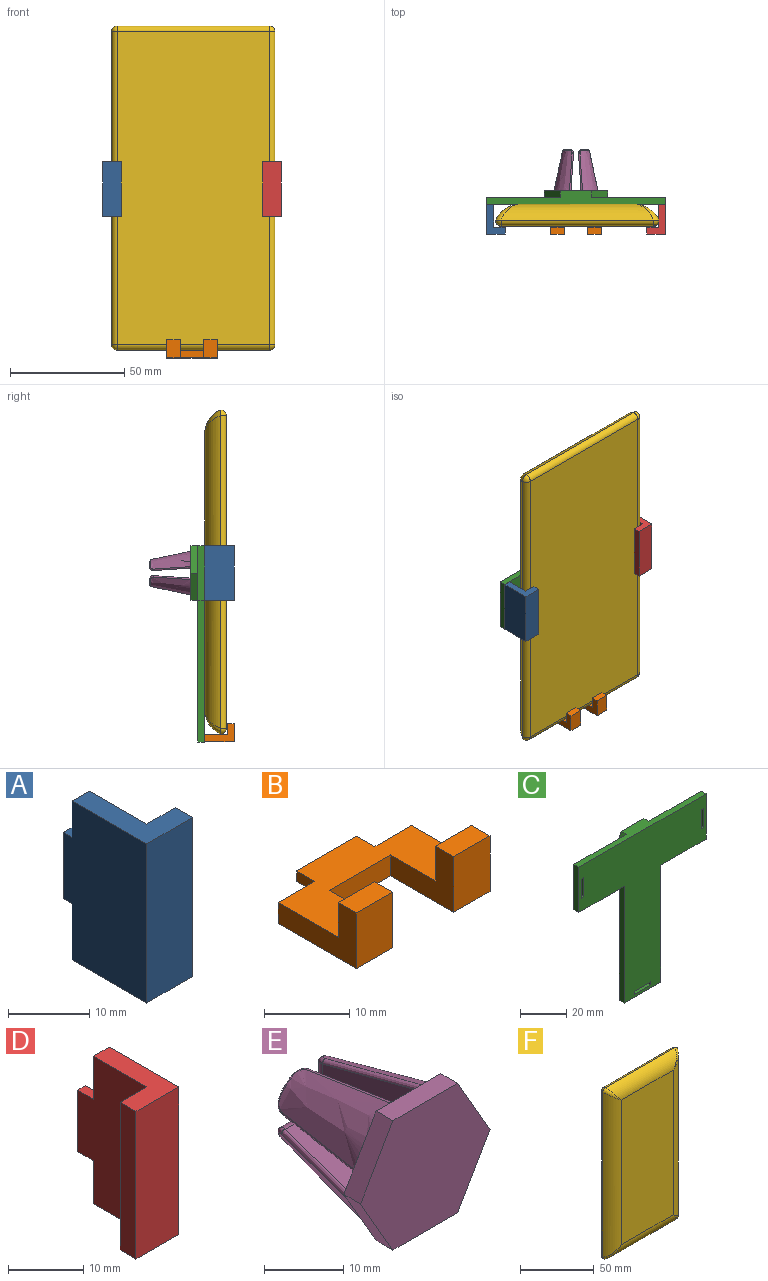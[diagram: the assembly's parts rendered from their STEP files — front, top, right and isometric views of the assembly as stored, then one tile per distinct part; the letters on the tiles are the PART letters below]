
ASSEMBLY  parts=6 mates=5
PART A: 12 faces, bbox 8x16x24 mm
  f0: plane 13x8mm, normal (0,0,-1), area 54mm2, adj f1,f4,f5,f6,f7,f11
  f1: plane 24x13mm, normal (1,0,0), area 270mm2, adj f0,f2,f3,f7,f8,f10,f11
  f2: plane 13x8mm, normal (0,0,1), area 54mm2, adj f1,f4,f5,f6,f7,f11
  f3: plane 10x1.5mm, normal (0,1,0), area 15mm2, adj f1,f8,f9,f10
  f4: plane 24x13mm, normal (-1,0,0), area 312mm2, adj f0,f2,f6,f11
  f5: plane 24x3mm, normal (1,0,0), area 72mm2, adj f0,f2,f6,f7
  f6: plane 24x8mm, normal (0,-1,0), area 192mm2, adj f0,f2,f4,f5
  f7: plane 24x5mm, normal (0,1,0), area 120mm2, adj f0,f1,f2,f5
  f8: plane 3x1.5mm, normal (0,0,1), area 4.5mm2, adj f1,f3,f9,f11
  f9: plane 10x3mm, normal (-1,0,0), area 30mm2, adj f3,f8,f10,f11
  f10: plane 3x1.5mm, normal (0,0,-1), area 4.5mm2, adj f1,f3,f9,f11
  f11: plane 24x3mm, normal (0,1,0), area 57mm2, adj f0,f1,f2,f4,f8,f9,f10
PART B: 18 faces, bbox 22.2x16x8 mm
  f0: plane 10x1.5mm, normal (0,1,0), area 15mm2, adj f1,f2,f3,f4
  f1: plane 22.2x13mm, normal (0,0,1), area 175.5mm2, adj f0,f3,f4,f5,f6,f7,f9,f12
  f2: plane 10x3mm, normal (0,0,-1), area 30mm2, adj f0,f3,f4,f5
  f3: plane 3x1.5mm, normal (-1,0,0), area 4.5mm2, adj f0,f1,f2,f5
  f4: plane 3x1.5mm, normal (1,0,0), area 4.5mm2, adj f0,f1,f2,f5
  f5: plane 22.2x3mm, normal (0,1,0), area 51.6mm2, adj f1,f2,f3,f4,f7,f8,f16
  f6: plane 10.5x8mm, normal (1,0,0), area 46.5mm2, adj f1,f8,f9,f10,f11,f17
  f7: plane 13x8mm, normal (-1,0,0), area 54mm2, adj f1,f5,f8,f9,f10,f11
  f8: plane 22.2x13mm, normal (0,0,-1), area 181.5mm2, adj f5,f6,f7,f11,f12,f15,f16,f17
  f9: plane 6x5mm, normal (0,1,0), area 30mm2, adj f1,f6,f7,f10
  f10: plane 6x3mm, normal (0,0,1), area 18mm2, adj f6,f7,f9,f11
  f11: plane 8x6mm, normal (0,-1,0), area 48mm2, adj f6,f7,f8,f10
  f12: plane 10.5x8mm, normal (-1,0,0), area 46.5mm2, adj f1,f8,f13,f14,f15,f17
  f13: plane 6x5mm, normal (0,1,0), area 30mm2, adj f1,f12,f14,f16
  f14: plane 6x3mm, normal (0,0,1), area 18mm2, adj f12,f13,f15,f16
  f15: plane 8x6mm, normal (0,-1,0), area 48mm2, adj f8,f12,f14,f16
  f16: plane 13x8mm, normal (1,0,0), area 54mm2, adj f1,f5,f8,f13,f14,f15
  f17: plane 10.2x3mm, normal (0,-1,0), area 30.6mm2, adj f1,f6,f8,f12
PART C: 35 faces, bbox 78.1x6x86 mm
  f0: plane 62x3mm, normal (-1,0,0), area 186mm2, adj f2,f3,f4,f5
  f1: plane 62x3mm, normal (1,0,0), area 186mm2, adj f2,f3,f4,f9
  f2: plane 22.2x3mm, normal (0,0,-1), area 66.6mm2, adj f0,f1,f3,f4
  f3: plane 86x78.1mm, normal (0,1,0), area 2703.5mm2, adj f0,f1,f2,f5,f6,f7,f8,f9
  f4: plane 86x78.1mm, normal (0,-1,0), area 3202.3mm2, adj f0,f1,f2,f5,f6,f7,f8,f9
  f5: plane 27.95x3mm, normal (0,0,-1), area 83.8mm2, adj f0,f3,f4,f8
  f6: plane 24x3mm, normal (1,0,0), area 72mm2, adj f3,f4,f7,f9
  f7: plane 78.1x6mm, normal (0,0,1), area 275.9mm2, adj f3,f4,f6,f8,f16,f17,f21
  f8: plane 24x3mm, normal (-1,0,0), area 72mm2, adj f3,f4,f5,f7
  f9: plane 27.95x3mm, normal (0,0,-1), area 83.8mm2, adj f1,f3,f4,f6
  f10: plane 10.1x5.83mm, normal (0.87,0,-0.5), area 35mm2, adj f11,f20,f21,f22
  f11: plane 10.1x5.83mm, normal (0.87,0,0.5), area 35mm2, adj f10,f12,f21,f22
  f12: plane 11.66x3mm, normal (0,0,1), area 35mm2, adj f11,f13,f21,f22
  f13: plane 10.1x5.83mm, normal (-0.87,0,0.5), area 35mm2, adj f12,f14,f21,f22
  f14: plane 10.1x5.83mm, normal (-0.87,0,-0.5), area 35mm2, adj f13,f20,f21,f22
  f15: plane 12x6.93mm, normal (-0.87,0,-0.5), area 41.6mm2, adj f3,f16,f19,f21
  f16: plane 12x6.93mm, normal (-0.87,0,0.5), area 41.6mm2, adj f3,f7,f15,f21
  f17: plane 12x6.93mm, normal (0.87,0,0.5), area 41.6mm2, adj f3,f7,f18,f21
  f18: plane 12x6.93mm, normal (0.87,0,-0.5), area 41.6mm2, adj f3,f17,f19,f21
  f19: plane 13.86x3mm, normal (0,0,-1), area 41.6mm2, adj f3,f15,f18,f21
  f20: plane 11.66x3mm, normal (0,0,-1), area 35mm2, adj f10,f14,f21,f22
  f21: plane 27.71x24mm, normal (0,1,0), area 145.5mm2, adj f7,f10,f11,f12,f13,f14,f15,f16
  f22: plane 23.33x20.2mm, normal (0,1,0), area 353.4mm2, adj f10,f11,f12,f13,f14,f20
  f23: plane 10.1x3mm, normal (1,0,0), area 30.3mm2, adj f3,f4,f24,f25
  f24: plane 3x1.6mm, normal (0,0,-1), area 4.8mm2, adj f3,f4,f23,f26
  f25: plane 3x1.6mm, normal (0,0,1), area 4.8mm2, adj f3,f4,f23,f26
  f26: plane 10.1x3mm, normal (-1,0,0), area 30.3mm2, adj f3,f4,f24,f25
  f27: plane 10.1x3mm, normal (0,0,1), area 30.3mm2, adj f3,f4,f28,f29
  f28: plane 3x1.6mm, normal (1,0,0), area 4.8mm2, adj f3,f4,f27,f30
  f29: plane 3x1.6mm, normal (-1,0,0), area 4.8mm2, adj f3,f4,f27,f30
  f30: plane 10.1x3mm, normal (0,0,-1), area 30.3mm2, adj f3,f4,f28,f29
  f31: plane 10.1x3mm, normal (1,0,0), area 30.3mm2, adj f3,f4,f32,f33
  f32: plane 3x1.6mm, normal (0,0,-1), area 4.8mm2, adj f3,f4,f31,f34
  f33: plane 3x1.6mm, normal (0,0,1), area 4.8mm2, adj f3,f4,f31,f34
  f34: plane 10.1x3mm, normal (-1,0,0), area 30.3mm2, adj f3,f4,f32,f33
PART D: 12 faces, bbox 8x16x24 mm
  f0: plane 13x8mm, normal (0,0,-1), area 54mm2, adj f1,f3,f5,f6,f7,f11
  f1: plane 24x13mm, normal (1,0,0), area 312mm2, adj f0,f4,f6,f11
  f2: plane 10x1.5mm, normal (0,1,0), area 15mm2, adj f3,f8,f9,f10
  f3: plane 24x13mm, normal (-1,0,0), area 270mm2, adj f0,f2,f4,f7,f8,f10,f11
  f4: plane 13x8mm, normal (0,0,1), area 54mm2, adj f1,f3,f5,f6,f7,f11
  f5: plane 24x3mm, normal (-1,0,0), area 72mm2, adj f0,f4,f6,f7
  f6: plane 24x8mm, normal (0,-1,0), area 192mm2, adj f0,f1,f4,f5
  f7: plane 24x5mm, normal (0,1,0), area 120mm2, adj f0,f3,f4,f5
  f8: plane 3x1.5mm, normal (0,0,-1), area 4.5mm2, adj f2,f3,f9,f11
  f9: plane 10x3mm, normal (1,0,0), area 30mm2, adj f2,f8,f10,f11
  f10: plane 3x1.5mm, normal (0,0,1), area 4.5mm2, adj f2,f3,f9,f11
  f11: plane 24x3mm, normal (0,1,0), area 57mm2, adj f0,f1,f3,f4,f8,f9,f10
PART E: 60 faces, bbox 23.2x23.4x20.6 mm
  f0: bspline ~17.61x8.12mm, area 143.4mm2, adj f4,f18,f19,f20,f48,f52
  f1: bspline ~17.61x8.12mm, area 143.4mm2, adj f4,f22,f23,f24,f43,f47
  f2: bspline ~17.61x8.12mm, area 143.4mm2, adj f4,f26,f27,f28,f38,f42
  f3: bspline ~17.61x8.12mm, area 143.4mm2, adj f4,f30,f31,f32,f33,f37
  f4: plane 23.15x20.06mm, normal (0,1,0), area 188.5mm2, adj f0,f1,f2,f3,f6,f7,f9,f10
  f5: plane 2.36x2.36mm, normal (0,1,0), area 3.3mm2, adj f31,f34,f36
  f6: plane 16.4x7.48mm, normal (-1,-0.07,0), area 85.4mm2, adj f4,f29,f32,f34
  f7: plane 16.4x7.48mm, normal (0,-0.07,-1), area 85.4mm2, adj f4,f29,f30,f36
  f8: plane 2.36x2.36mm, normal (0,1,0), area 3.3mm2, adj f27,f39,f41
  f9: plane 16.4x7.48mm, normal (1,-0.07,0), area 85.4mm2, adj f4,f25,f28,f39
  f10: plane 16.4x7.48mm, normal (0,-0.07,-1), area 85.4mm2, adj f4,f25,f26,f41
  f11: plane 2.36x2.36mm, normal (0,1,0), area 3.3mm2, adj f23,f44,f46
  f12: plane 16.4x7.48mm, normal (-1,-0.07,0), area 85.4mm2, adj f4,f21,f24,f44
  f13: plane 16.4x7.48mm, normal (0,-0.07,1), area 85.4mm2, adj f4,f21,f22,f46
  f14: plane 2.36x2.36mm, normal (0,1,0), area 3.3mm2, adj f19,f49,f51
  f15: plane 16.4x7.48mm, normal (0,-0.07,1), area 85.4mm2, adj f4,f17,f20,f49
  f16: plane 16.4x7.48mm, normal (1,-0.07,0), area 85.4mm2, adj f4,f17,f18,f51
  f17: cylinder r=0.5mm len=16.41mm, axis (-0.07,-1,-0.07), area 12.9mm2, adj f4,f15,f16,f50
  f18: bspline ~22.72x5.45mm, area 15.7mm2, adj f0,f4,f16,f52
  f19: bspline ~3.89x3.54mm, area 2.4mm2, adj f0,f14,f48,f52
  f20: bspline ~22.72x5.45mm, area 15.7mm2, adj f0,f4,f15,f48
  f21: cylinder r=0.5mm len=16.41mm, axis (0.07,-1,-0.07), area 12.9mm2, adj f4,f12,f13,f45
  f22: bspline ~22.72x5.45mm, area 15.7mm2, adj f1,f4,f13,f47
  f23: bspline ~3.89x3.54mm, area 2.4mm2, adj f1,f11,f43,f47
  f24: bspline ~22.72x5.45mm, area 15.7mm2, adj f1,f4,f12,f43
  f25: cylinder r=0.5mm len=16.41mm, axis (-0.07,-1,0.07), area 12.9mm2, adj f4,f9,f10,f40
  f26: bspline ~22.72x5.45mm, area 15.7mm2, adj f2,f4,f10,f42
  f27: bspline ~3.89x3.54mm, area 2.4mm2, adj f2,f8,f38,f42
  f28: bspline ~22.72x5.45mm, area 15.7mm2, adj f2,f4,f9,f38
  f29: cylinder r=0.5mm len=16.41mm, axis (-0.07,1,-0.07), area 12.9mm2, adj f4,f6,f7,f35
  f30: bspline ~20.18x4.91mm, area 15.7mm2, adj f3,f4,f7,f37
  f31: bspline ~3.62x3.43mm, area 2.4mm2, adj f3,f5,f33,f37
  f32: bspline ~20.18x4.91mm, area 15.7mm2, adj f3,f4,f6,f33
  f33: bspline ~2.03x1.75mm, area 1.9mm2, adj f3,f31,f32,f34
  f34: cylinder r=1.5mm len=4mm, axis (0,0,-1), area 7.8mm2, adj f5,f6,f33,f35
  f35: bspline ~1.76x1.5mm, area 0.9mm2, adj f29,f34,f36
  f36: cylinder r=1.5mm len=4mm, axis (-1,0,0), area 7.8mm2, adj f5,f7,f35,f37
  f37: bspline ~1.99x1.93mm, area 1.9mm2, adj f3,f30,f31,f36
  f38: bspline ~1.99x1.93mm, area 1.9mm2, adj f2,f27,f28,f39
  f39: cylinder r=1.5mm len=4mm, axis (0,0,-1), area 7.8mm2, adj f8,f9,f38,f40
  f40: bspline ~1.76x1.5mm, area 0.9mm2, adj f25,f39,f41
  f41: cylinder r=1.5mm len=4mm, axis (1,0,0), area 7.8mm2, adj f8,f10,f40,f42
  f42: bspline ~2.03x1.75mm, area 1.9mm2, adj f2,f26,f27,f41
  f43: bspline ~1.99x1.93mm, area 1.9mm2, adj f1,f23,f24,f44
  f44: cylinder r=1.5mm len=4mm, axis (0,0,1), area 7.8mm2, adj f11,f12,f43,f45
  f45: bspline ~1.76x1.5mm, area 0.9mm2, adj f21,f44,f46
  f46: cylinder r=1.5mm len=4mm, axis (-1,0,0), area 7.8mm2, adj f11,f13,f45,f47
  f47: bspline ~2.03x1.75mm, area 1.9mm2, adj f1,f22,f23,f46
  f48: bspline ~1.99x1.93mm, area 1.9mm2, adj f0,f19,f20,f49
  f49: cylinder r=1.5mm len=4mm, axis (1,0,0), area 7.8mm2, adj f14,f15,f48,f50
  f50: bspline ~1.76x1.5mm, area 0.9mm2, adj f17,f49,f51
  f51: cylinder r=1.5mm len=4mm, axis (0,0,1), area 7.8mm2, adj f14,f16,f50,f52
  f52: bspline ~2.03x1.75mm, area 1.9mm2, adj f0,f18,f19,f51
  f53: plane 11.55x3mm, normal (0,0,1), area 34.6mm2, adj f4,f54,f58,f59
  f54: plane 10x5.77mm, normal (0.87,0,0.5), area 34.6mm2, adj f4,f53,f55,f59
  f55: plane 10x5.77mm, normal (0.87,0,-0.5), area 34.6mm2, adj f4,f54,f56,f59
  f56: plane 11.55x3mm, normal (0,0,-1), area 34.6mm2, adj f4,f55,f57,f59
  f57: plane 10x5.77mm, normal (-0.87,0,-0.5), area 34.6mm2, adj f4,f56,f58,f59
  f58: plane 10x5.77mm, normal (-0.87,0,0.5), area 34.6mm2, adj f4,f53,f57,f59
  f59: plane 23.09x20mm, normal (0,-1,0), area 346.4mm2, adj f53,f54,f55,f56,f57,f58
PART F: 18 faces, bbox 71.6x9.5x142 mm
  f0: plane 120.18x49.78mm, normal (0,-1,0), area 5983mm2, adj f10,f13,f14,f17
  f1: plane 137x66.6mm, normal (0,1,0), area 9124.2mm2, adj f3,f4,f7,f8
  f2: sphere r=2.5mm, area 9.8mm2, adj f3,f4,f11
  f3: cylinder r=2.5mm len=66.6mm, axis (-1,0,0), area 261.5mm2, adj f1,f2,f5,f13
  f4: cylinder r=2.5mm len=137mm, axis (0,0,-1), area 538mm2, adj f1,f2,f6,f10
  f5: sphere r=2.5mm, area 13.4mm2, adj f3,f7,f15
  f6: sphere r=2.5mm, area 9.8mm2, adj f4,f8,f12
  f7: cylinder r=2.5mm len=137mm, axis (0,0,1), area 538mm2, adj f1,f5,f9,f17
  f8: cylinder r=2.5mm len=66.6mm, axis (1,0,0), area 261.5mm2, adj f1,f6,f9,f14
  f9: sphere r=2.5mm, area 6.2mm2, adj f7,f8,f16
  f10: cylinder r=12mm len=137mm, axis (0,0,-1), area 1760.7mm2, adj f0,f4,f11,f12
  f11: bspline ~10.91x10.91mm, area 22mm2, adj f2,f10,f13
  f12: bspline ~10.91x10.91mm, area 22mm2, adj f6,f10,f14
  f13: cylinder r=12mm len=66.6mm, axis (1,0,0), area 796.8mm2, adj f0,f3,f11,f15
  f14: cylinder r=12mm len=66.6mm, axis (1,0,0), area 796.8mm2, adj f0,f8,f12,f16
  f15: bspline ~10.91x10.91mm, area 22mm2, adj f5,f13,f17
  f16: bspline ~10.91x10.91mm, area 22mm2, adj f9,f14,f17
  f17: cylinder r=12mm len=137mm, axis (0,0,-1), area 1760.7mm2, adj f0,f7,f15,f16
PLACE A t=(-81.2,-40.39,27.55)mm
PLACE B t=(-94.2,-40.39,40.65)mm
PLACE C t=(-94.2,-40.39,27.55)mm
PLACE D t=(-107.2,-40.39,27.55)mm
PLACE E t=(-94.2,-57.39,27.55)mm
PLACE F rot(axis=(1,0,0),180deg) t=(-232.27,-69.89,-8.84)mm
MATE fastened B.f0 <-> C.f3  axis (0,1,0) through (-94.2,-57.39,-43.35)mm
MATE fastened E.f59 <-> C.f22  axis (0,-1,0) through (-94.2,-57.39,27.55)mm
MATE planar C.f4 <-> F.f0  axis (0,-1,0) through (-94.2,-60.39,9.43)mm
MATE fastened D.f2 <-> C.f3  axis (0,1,0) through (-56.65,-57.39,27.55)mm
MATE fastened A.f3 <-> C.f3  axis (0,1,0) through (-131.75,-57.39,27.55)mm
